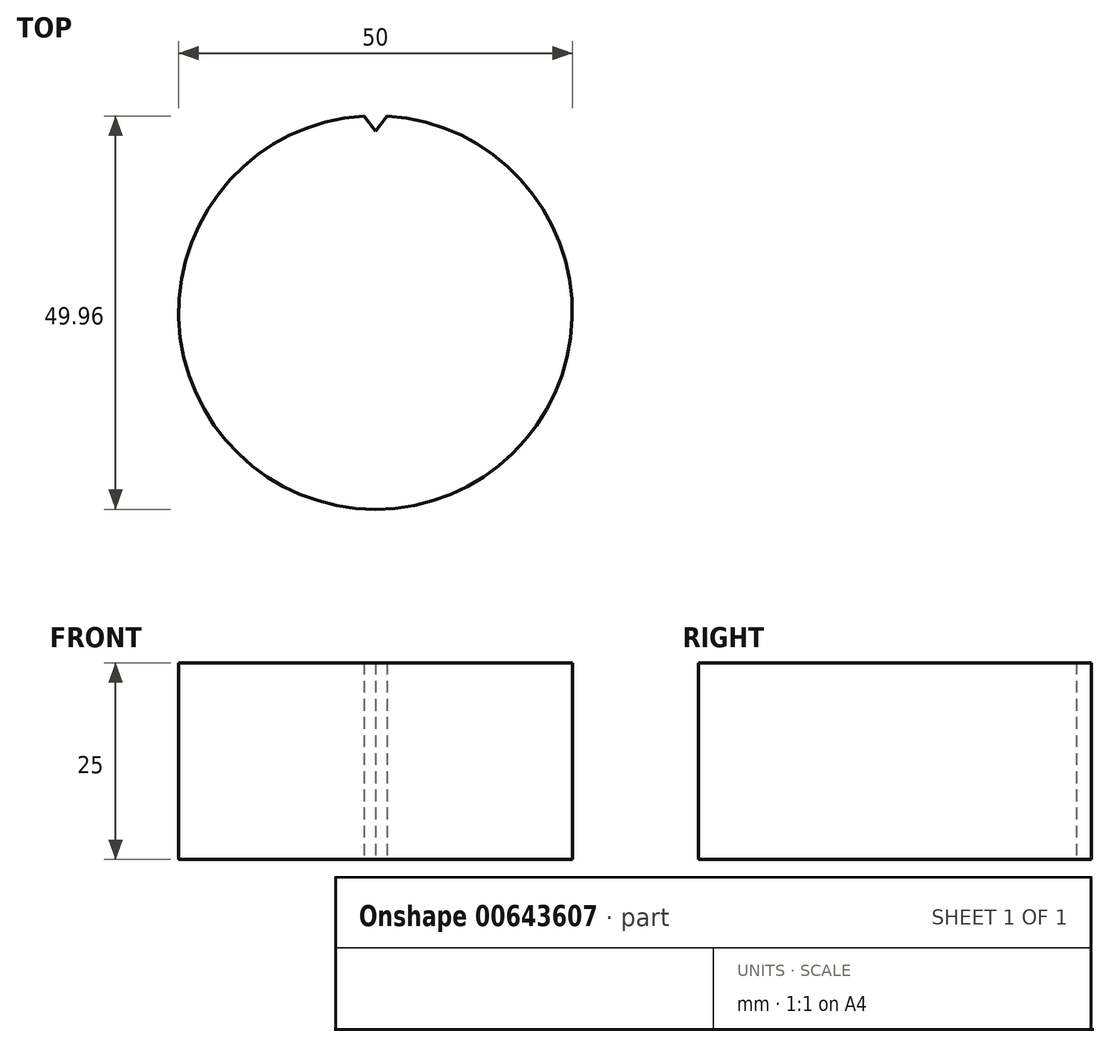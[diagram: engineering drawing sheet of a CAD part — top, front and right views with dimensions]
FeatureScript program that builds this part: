
annotation { "Feature Type Name" : "Feature", "Feature Type Description" : "" }
export const myFeature = defineFeature(function(context is Context, id is Id, definition is map)
    precondition{}
    {
        {
            var Q0;
            Q0=qCreatedBy(makeId("Top.planeOp"),FACE);
            var sketch = newSketch(context, id + "F0", { "sketchPlane" : qUnion([Q0])});
            skCircle(sketch, "E0", {"center": v(0, 0) * mm, "radius": 25 * mm});
            skLineSegment(sketch, "E1", {"start": v(0, 25) * mm, "end": v(0, 23.04) * mm});
            skLineSegment(sketch, "E2", {"start": v(0, 23.04) * mm, "end": v(1.48, 24.96) * mm});
            skLineSegment(sketch, "E3", {"start": v(1.48, 24.96) * mm, "end": v(0, 23.04) * mm});
            skLineSegment(sketch, "E4", {"start": v(0, 23.04) * mm, "end": v(-1.48, 24.96) * mm});
            skSolve(sketch);
        }
        {
            var Q0;
            {var subQ0=sQuery(id+"F0.wireOp",EDGE,"E0");var subQ1=makeQuery(id+"F0.imprint","INTERSECT",VERTEX,{"derivedFrom":[subQ0,sQuery(id+"F0.wireOp",EDGE,"53tO8hcr-aGsh-EoXn-KGiG-CWoGSQn3GmJp")]});Q0=makeQuery(id+"F0.imprint","IMPRINT",FACE,{"disambiguationData":[TD([[makeQuery(id+"F0.imprint","IMPRINT",EDGE,{"disambiguationData":[TD([[subQ1,1.0]])],"derivedFrom":subQ0}),1.0]])]});}
            extrude(context, id + "F1", {"entities" : qUnion([Q0]), "depth" : 25 * mm, "offsetDistance" : 25 * mm});
        }
        {
            var Q0;
            {var subQ0=sQuery(id+"F0.wireOp",EDGE,"E1");Q0=makeQuery(id+"F0.imprint","IMPRINT",FACE,{"disambiguationData":[TD([[makeQuery(id+"F0.imprint","IMPRINT",EDGE,{"derivedFrom":subQ0}),-1.0]])]});}
            var Q1;
            {var subQ0=sQuery(id+"F0.wireOp",EDGE,"E1");Q1=makeQuery(id+"F0.imprint","IMPRINT",FACE,{"disambiguationData":[TD([[makeQuery(id+"F0.imprint","IMPRINT",EDGE,{"derivedFrom":subQ0}),1.0]])]});}
            extrude(context, id + "F2", {"entities" : qUnion([Q0, Q1]), "operationType" : NewBodyOperationType.REMOVE, "depth" : 30 * mm, "offsetDistance" : 25 * mm});
        }
    });
